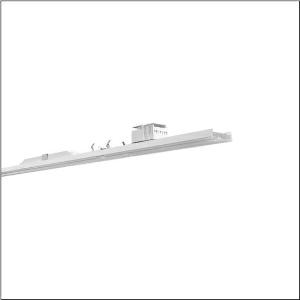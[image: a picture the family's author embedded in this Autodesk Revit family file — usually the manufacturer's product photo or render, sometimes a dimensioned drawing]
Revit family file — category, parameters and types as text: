
# Revit family: licross_r__21_recessed_mo_52tl18dnd75f_1d51
name_source: partatom
category: Lighting Fixtures
units: mm (PartAtom-declared; Revit-internal decimal feet)

## family parameters
Cut with Voids When Loaded = No
Host = Face
Light Source = No
Part Type = Normal
Room Calculation Point = No
Round Connector Dimension = Use Diameter
Shared = No

## types (1)
- --- (1 x LED, 7730 lm, 59.8 W, 4000K)
    Apparent Load = 60 VA
    CIE Flux Codes = 79 95 99 100 100
    Color Rendering = 90
    Color Temperature = 4000K
    Default Elevation = 1800 mm
    Description = Licross® 21 Recessed MO, luminaire insert, of sheet steel, galvanised, coil coated, white, length: 1.500mm, width: 66mm, height: 67mm, LED rated luminous flux: 7.730lm, light colour: 940, control gear: DALI 2, control gear: ECG DALI, with plug, 5-pole, with phase selection, mains connection: 220..240V, AC, 50/60Hz, rated input power: 61W, halogen-free wiring, primary optical cover: cover, of PMMA, light emission: direct distribution, primary light characteristic: symmetric, protection rating (complete): IP40, insulation class (complete): insulation class I (protective earthing), certification: CE, ENEC, VDE, UKCA, protection symbol: D if used in an environment without relevant dust loads with corresponding accessories, impact resistance: IK06, permissible ambient temperature for indoor applications: -25..+35°C, corresponds to IFS (International Featured Standards) requirements for safety and quality in the food industry, reducing of maximum allowable ambient temperature of 5°C with ceiling mounting, LABS conformity tested according to VDMA 24364:2018-05, packaging unit: 1 piece
    Height = 58 mm
    Lamp = 1 x LED
    Lamp Light Flux = 7730 lm
    Lamp Power = 59.8 W
    Lamp count = 1
    Length = 1500 mm
    Luminous efficacy = 129 lm/W
    Manufacturer = Siteco
    ModVariant = No
    Model = 52TL18DND75F
    Mounting Place = Ceiling
    Mounting Type = Pendant
    Number of Poles = 1
    OnlyDefault = Yes
    Power Factor = 1
    Product Name = Licross® 21 Recessed MO
    Product group = luminaire insert
    ProductGroupID = 901
    Protection Class = Protection class I
    Protection Degree = IP 40
    RLX_Detail_Level = 1
    RLX_Emergency_Light_Flux = 0 lm
    RLX_Emergency_Type = 0
    RLX_Emergency_Type_DB = No
    RlxData = <blob elided: 22665 chars, md5=55548f26>
    Socket = socket
    Standby Power = 0 W
    System Light Flux = 7730 lm
    System Power = 60 W
    Type Comments = factory setting: luminous flux: 100 % | dim-lin: 254 | 405 mA
    Type Image = l_1296935.jpg
    URL = http://relux.com
    VarID = @adj_117457
    Voltage = 0 V
    Weight = 0.00 kg
    Width = 66 mm

## geometry (parser evidence)
native form markers: Blend x4, Sweep x11
no freeform markers — native parametric forms only
